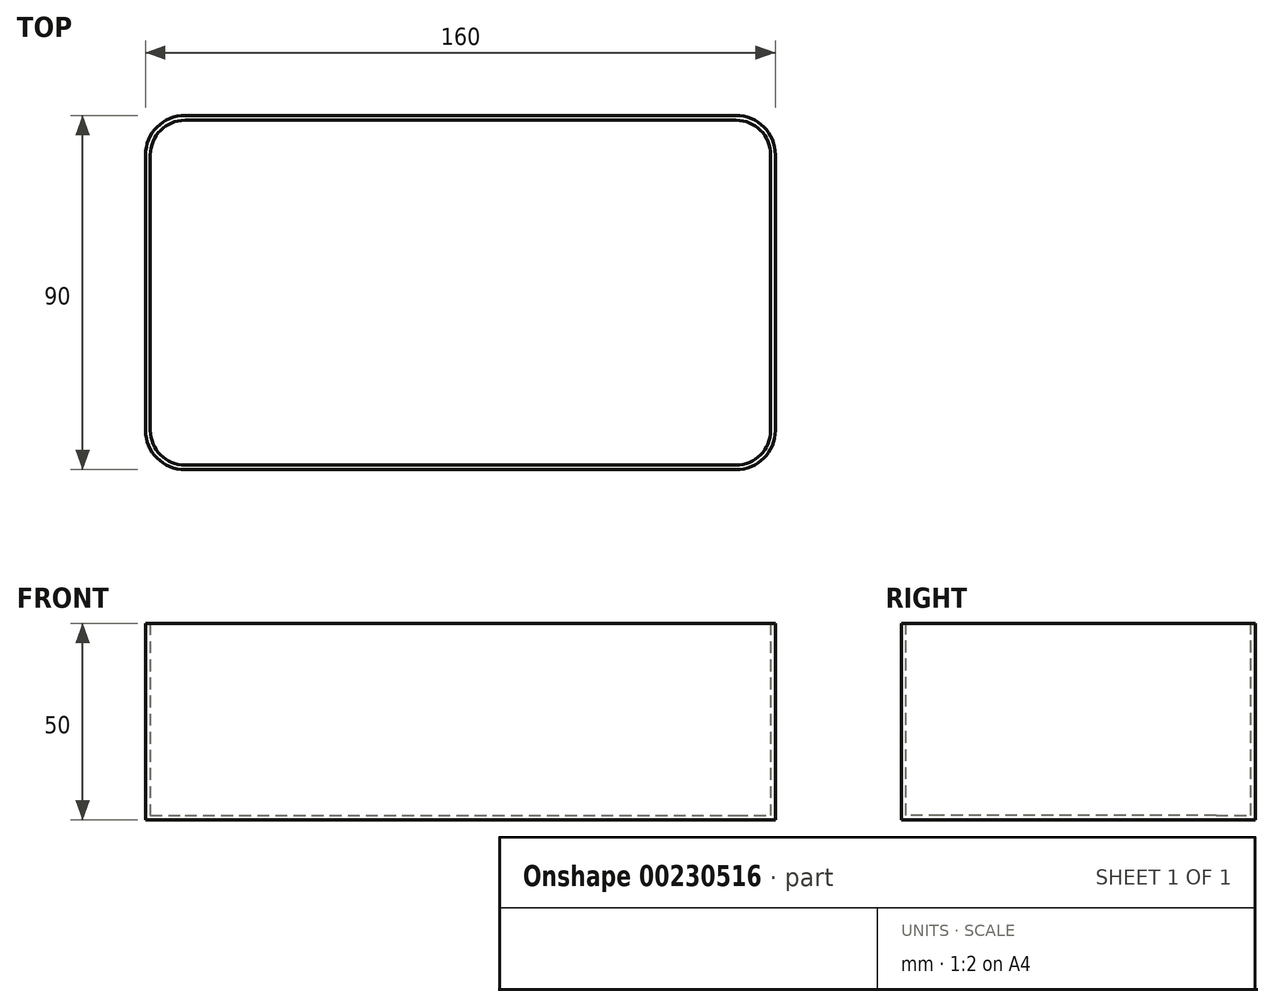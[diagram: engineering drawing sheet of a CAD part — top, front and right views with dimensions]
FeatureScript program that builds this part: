
annotation { "Feature Type Name" : "Feature", "Feature Type Description" : "" }
export const myFeature = defineFeature(function(context is Context, id is Id, definition is map)
    precondition{}
    {
        {
            var Q0;
            Q0=qCreatedBy(makeId("Top.planeOp"),FACE);
            var sketch = newSketch(context, id + "F0", { "sketchPlane" : qUnion([Q0])});
            skLineSegment(sketch, "E0.bottom", {"start": v(-107.19, 40.26) * mm, "end": v(32.81, 40.26) * mm});
            skLineSegment(sketch, "E0.top", {"start": v(-107.19, -49.74) * mm, "end": v(32.81, -49.74) * mm});
            skLineSegment(sketch, "E0.left", {"start": v(-117.19, 30.26) * mm, "end": v(-117.19, -39.74) * mm});
            skLineSegment(sketch, "E0.right", {"start": v(42.81, 30.26) * mm, "end": v(42.81, -39.74) * mm});
            skPoint(sketch, "E1.visualSharp", {"position": v(-117.19, 40.26) * mm});
            skArc(sketch, "E1.filletArc", {"start": v(-107.19, 40.26) * mm, "mid": v(-114.26, 37.34) * mm, "end": v(-117.19, 30.26) * mm});
            skPoint(sketch, "E2.visualSharp", {"position": v(-117.19, -49.74) * mm});
            skArc(sketch, "E2.filletArc", {"start": v(-117.19, -39.74) * mm, "mid": v(-114.26, -46.8) * mm, "end": v(-107.19, -49.74) * mm});
            skPoint(sketch, "E3.visualSharp", {"position": v(42.81, -49.74) * mm});
            skArc(sketch, "E3.filletArc", {"start": v(32.81, -49.74) * mm, "mid": v(39.88, -46.8) * mm, "end": v(42.81, -39.74) * mm});
            skPoint(sketch, "E4.visualSharp", {"position": v(42.81, 40.26) * mm});
            skArc(sketch, "E4.filletArc", {"start": v(42.81, 30.26) * mm, "mid": v(39.88, 37.34) * mm, "end": v(32.81, 40.26) * mm});
            skSolve(sketch);
        }
        {
            var Q0;
            Q0 = qSketchRegion(id + "F0", true);
            extrude(context, id + "F1", {"entities" : qUnion([Q0]), "depth" : 50 * mm});
        }
        {
            var Q0;
            Q0=makeQuery(id+"F1.opExtrude","CAP_FACE",FACE,{"disambiguationData":[OSD([sQuery(id+"F0.wireOp",EDGE,"E0.bottom"),sQuery(id+"F0.wireOp",EDGE,"E0.top"),sQuery(id+"F0.wireOp",EDGE,"E0.left"),sQuery(id+"F0.wireOp",EDGE,"E0.right"),sQuery(id+"F0.wireOp",EDGE,"E1.filletArc"),sQuery(id+"F0.wireOp",EDGE,"E2.filletArc"),sQuery(id+"F0.wireOp",EDGE,"E3.filletArc"),sQuery(id+"F0.wireOp",EDGE,"E4.filletArc")])],"isStart":false});
            shell(context, id + "F2", {"entities" : qUnion([Q0]), "thickness" : 1.2 * mm});
        }
    });
